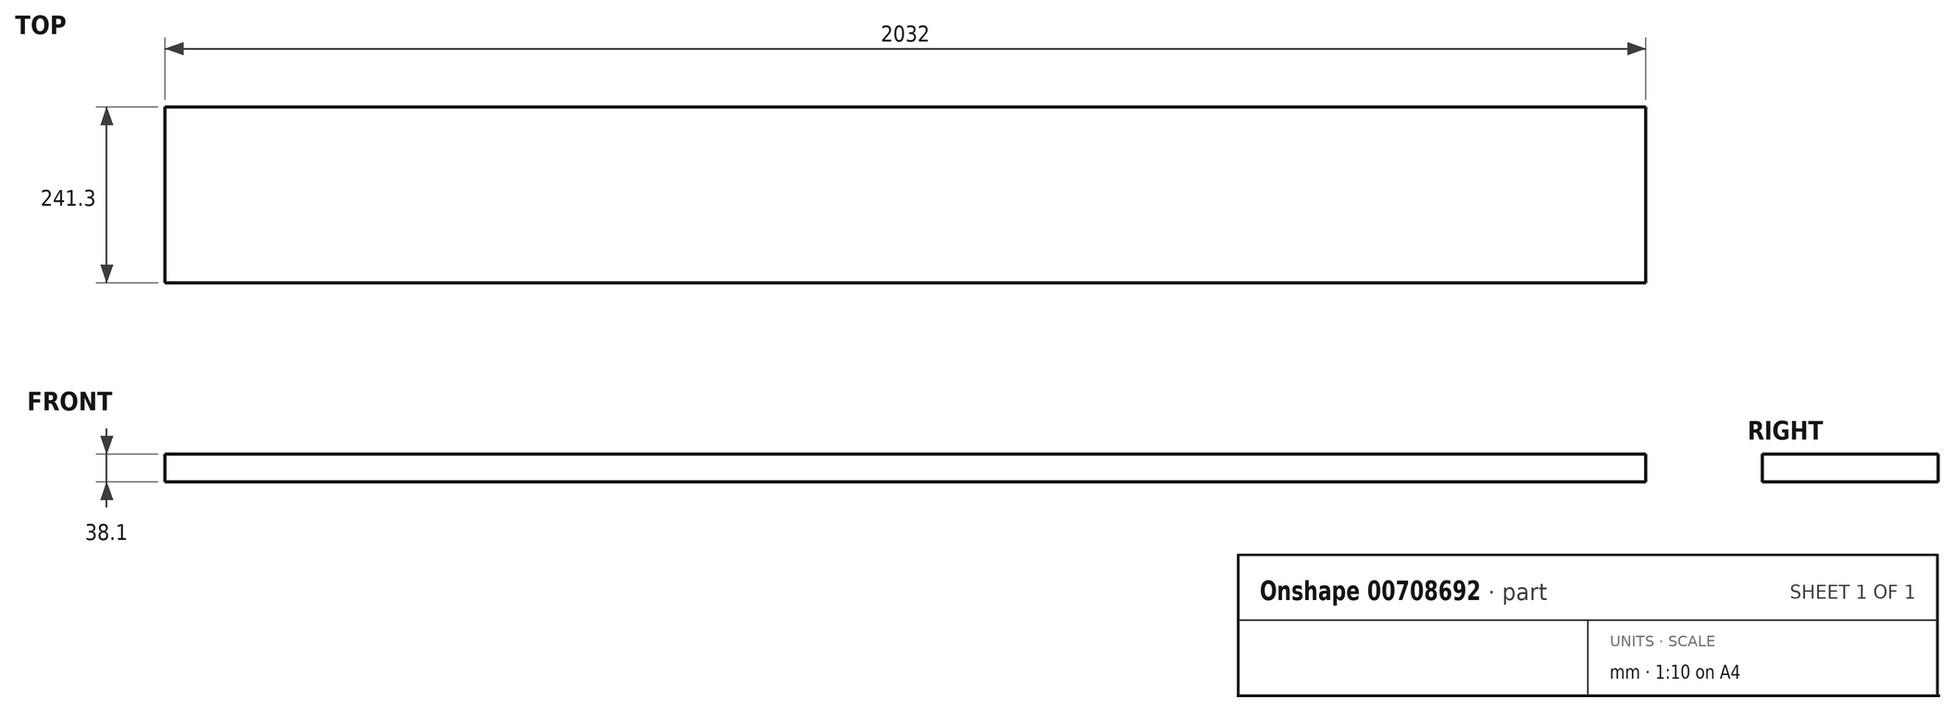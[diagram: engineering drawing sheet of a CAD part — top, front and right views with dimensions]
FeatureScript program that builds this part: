
annotation { "Feature Type Name" : "Feature", "Feature Type Description" : "" }
export const myFeature = defineFeature(function(context is Context, id is Id, definition is map)
    precondition{}
    {
        {
            var Q0;
            Q0=qCreatedBy(makeId("Right.planeOp"),FACE);
            var sketch = newSketch(context, id + "F0", { "sketchPlane" : qUnion([Q0])});
            skLineSegment(sketch, "E0.bottom", {"start": v(120.65, -19.05) * mm, "end": v(-120.65, -19.05) * mm});
            skLineSegment(sketch, "E0.top", {"start": v(120.65, 19.05) * mm, "end": v(-120.65, 19.05) * mm});
            skLineSegment(sketch, "E0.left", {"start": v(120.65, -19.05) * mm, "end": v(120.65, 19.05) * mm});
            skLineSegment(sketch, "E0.right", {"start": v(-120.65, -19.05) * mm, "end": v(-120.65, 19.05) * mm});
            skPoint(sketch, "E0.middle", {"position": v(0, 0) * mm});
            skSolve(sketch);
        }
        {
            var Q0;
            Q0=makeQuery(id+"F0.imprint","IMPRINT",FACE,{"disambiguationData":[TD([[makeQuery(id+"F0.imprint","IMPRINT",EDGE,{"derivedFrom":sQuery(id+"F0.wireOp",EDGE,"E0.bottom")}),-1.0]])]});
            extrude(context, id + "F1", {"entities" : qUnion([Q0]), "endBound" : BoundingType.SYMMETRIC, "depth" : 2032 * mm, "offsetDistance" : 25.4 * mm});
        }
    });
